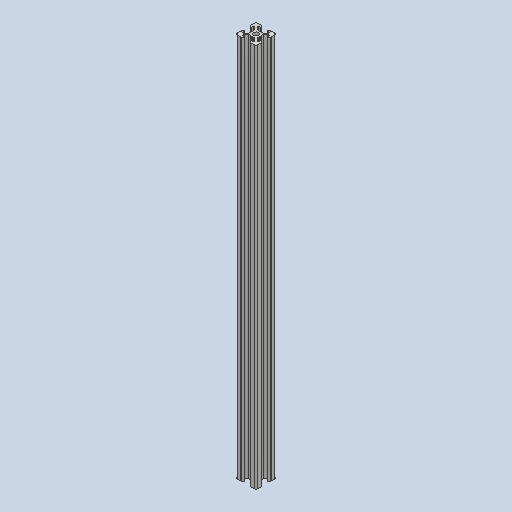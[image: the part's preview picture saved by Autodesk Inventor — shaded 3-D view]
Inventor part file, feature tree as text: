
AUTODESK INVENTOR PART (.ipt)
format: ipt  version: 2025.2 (Build 292293000, 293)  size: 406,016 bytes
history: native  units: mm
features: other x1, extrude x1, sketch x1
ambient origin geometry x8: Origin, YZ Plane, XZ Plane, XY Plane, X Axis, Y Axis, Z Axis, Center Point
bodies: Body1 (feature_tree)
feature tree (3):
  other  "Твердое тело1"
  extrude  "Выдавливание1"  Depth=0.25mm
  sketch  "Эскиз1"
